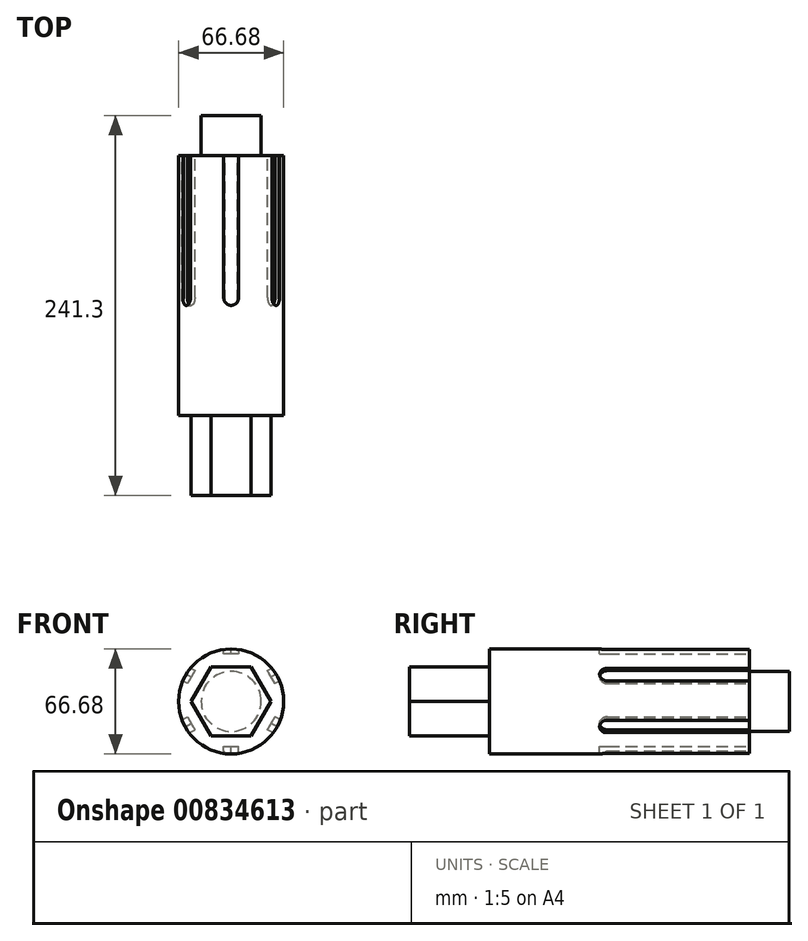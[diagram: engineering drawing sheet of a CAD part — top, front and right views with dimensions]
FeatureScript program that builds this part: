
annotation { "Feature Type Name" : "Feature", "Feature Type Description" : "" }
export const myFeature = defineFeature(function(context is Context, id is Id, definition is map)
    precondition{}
    {
        {
            var Q0;
            Q0=qCreatedBy(makeId("Front.planeOp"),FACE);
            var sketch = newSketch(context, id + "F0", { "sketchPlane" : qUnion([Q0])});
            skCircle(sketch, "E0.cCircle", {"center": v(0, 0) * mm, "radius": 25.4 * mm, "construction": true});
            skLineSegment(sketch, "E0.0", {"start": v(12.7, -22) * mm, "end": v(-12.7, -22) * mm});
            skLineSegment(sketch, "E0.1", {"start": v(-12.7, -22) * mm, "end": v(-25.4, 0) * mm});
            skLineSegment(sketch, "E0.2", {"start": v(-25.4, 0) * mm, "end": v(-12.7, 22) * mm});
            skLineSegment(sketch, "E0.3", {"start": v(-12.7, 22) * mm, "end": v(12.7, 22) * mm});
            skLineSegment(sketch, "E0.4", {"start": v(12.7, 22) * mm, "end": v(25.4, 0) * mm});
            skLineSegment(sketch, "E0.5", {"start": v(25.4, 0) * mm, "end": v(12.7, -22) * mm});
            skSolve(sketch);
        }
        {
            var Q0;
            Q0=makeQuery(id+"F0.imprint","IMPRINT",FACE,{"disambiguationData":[TD([[makeQuery(id+"F0.imprint","IMPRINT",EDGE,{"derivedFrom":sQuery(id+"F0.wireOp",EDGE,"E0.0")}),-1.0]])]});
            extrude(context, id + "F1", {"entities" : qUnion([Q0]), "depth" : 50.8 * mm, "offsetDistance" : 25.4 * mm});
        }
        {
            var Q0;
            Q0=makeQuery(id+"F1.opExtrude","CAP_FACE",FACE,{"disambiguationData":[OSD([sQuery(id+"F0.wireOp",EDGE,"E0.0"),sQuery(id+"F0.wireOp",EDGE,"E0.1"),sQuery(id+"F0.wireOp",EDGE,"E0.2"),sQuery(id+"F0.wireOp",EDGE,"E0.3"),sQuery(id+"F0.wireOp",EDGE,"E0.4"),sQuery(id+"F0.wireOp",EDGE,"E0.5")])],"isStart":true});
            var sketch = newSketch(context, id + "F2", { "sketchPlane" : qUnion([Q0])});
            skCircle(sketch, "E1", {"center": v(0, 0) * mm, "radius": 33.34 * mm});
            skSolve(sketch);
        }
        {
            var Q0;
            Q0 = qSketchRegion(id + "F2", true);
            extrude(context, id + "F3", {"entities" : qUnion([Q0]), "operationType" : NewBodyOperationType.ADD, "depth" : 165.1 * mm, "offsetDistance" : 25.4 * mm});
        }
        {
            var Q0;
            Q0=makeQuery(id+"F3.opExtrude","CAP_FACE",FACE,{"disambiguationData":[OSD([sQuery(id+"F2.wireOp",EDGE,"E1")])],"isStart":false});
            var sketch = newSketch(context, id + "F4", { "sketchPlane" : qUnion([Q0])});
            skCircle(sketch, "E2", {"center": v(0, 0) * mm, "radius": 19.05 * mm});
            skSolve(sketch);
        }
        {
            var Q0;
            Q0 = qSketchRegion(id + "F4", true);
            extrude(context, id + "F5", {"entities" : qUnion([Q0]), "operationType" : NewBodyOperationType.ADD, "depth" : 25.4 * mm, "offsetDistance" : 25.4 * mm});
        }
        {
            var Q0;
            Q0=makeQuery(id+"F3.opExtrude","CAP_FACE",FACE,{"disambiguationData":[OSD([sQuery(id+"F2.wireOp",EDGE,"E1")])],"isStart":false});
            var sketch = newSketch(context, id + "F6", { "sketchPlane" : qUnion([Q0])});
            skLineSegment(sketch, "E3", {"start": v(0, 0) * mm, "end": v(0, 60.33) * mm, "construction": true});
            skLineSegment(sketch, "E4", {"start": v(-4.76, 33) * mm, "end": v(-4.76, 30.16) * mm});
            skLineSegment(sketch, "E5", {"start": v(-4.76, 30.16) * mm, "end": v(4.76, 30.16) * mm});
            skLineSegment(sketch, "E6", {"start": v(4.76, 30.16) * mm, "end": v(4.76, 33) * mm});
            skPoint(sketch, "E7", {"position": v(0, 30.16) * mm});
            skArc(sketch, "E8", {"start": v(4.76, 33) * mm, "mid": v(0, 36.72) * mm, "end": v(-4.76, 33) * mm});
            skPoint(sketch, "E9", {"position": v(0, 33.34) * mm});
            skLineSegment(sketch, "E10.1.0", {"start": v(25.51, 21.02) * mm, "end": v(23.06, 19.6) * mm});
            skLineSegment(sketch, "E10.1.1", {"start": v(23.06, 19.6) * mm, "end": v(27.82, 11.35) * mm});
            skArc(sketch, "E10.1.2", {"start": v(30.27, 12.77) * mm, "mid": v(31.12, 18.75) * mm, "end": v(25.51, 21.02) * mm});
            skLineSegment(sketch, "E10.1.3", {"start": v(-0.68, 0.4) * mm, "end": v(51.56, 30.56) * mm, "construction": true});
            skLineSegment(sketch, "E10.2.0", {"start": v(30.27, -11.2) * mm, "end": v(27.82, -9.78) * mm});
            skLineSegment(sketch, "E10.2.1", {"start": v(27.82, -9.78) * mm, "end": v(23.06, -18.02) * mm});
            skArc(sketch, "E10.2.2", {"start": v(25.51, -19.44) * mm, "mid": v(31.12, -17.18) * mm, "end": v(30.27, -11.2) * mm});
            skLineSegment(sketch, "E10.2.3", {"start": v(-0.68, 1.18) * mm, "end": v(51.56, -28.98) * mm, "construction": true});
            skLineSegment(sketch, "E10.3.0", {"start": v(4.76, -31.42) * mm, "end": v(4.76, -28.59) * mm});
            skLineSegment(sketch, "E10.3.1", {"start": v(4.76, -28.59) * mm, "end": v(-4.76, -28.59) * mm});
            skArc(sketch, "E10.3.2", {"start": v(-4.76, -31.42) * mm, "mid": v(0, -35.14) * mm, "end": v(4.76, -31.42) * mm});
            skLineSegment(sketch, "E10.3.3", {"start": v(0, 1.57) * mm, "end": v(0, -58.75) * mm, "construction": true});
            skLineSegment(sketch, "E10.4.0", {"start": v(-25.51, -19.44) * mm, "end": v(-23.06, -18.02) * mm});
            skLineSegment(sketch, "E10.4.1", {"start": v(-23.06, -18.02) * mm, "end": v(-27.82, -9.78) * mm});
            skArc(sketch, "E10.4.2", {"start": v(-30.27, -11.2) * mm, "mid": v(-31.12, -17.18) * mm, "end": v(-25.51, -19.44) * mm});
            skLineSegment(sketch, "E10.4.3", {"start": v(0.68, 1.18) * mm, "end": v(-51.56, -28.98) * mm, "construction": true});
            skLineSegment(sketch, "E10.5.0", {"start": v(-30.27, 12.77) * mm, "end": v(-27.82, 11.35) * mm});
            skLineSegment(sketch, "E10.5.1", {"start": v(-27.82, 11.35) * mm, "end": v(-23.06, 19.6) * mm});
            skArc(sketch, "E10.5.2", {"start": v(-25.51, 21.02) * mm, "mid": v(-31.12, 18.75) * mm, "end": v(-30.27, 12.77) * mm});
            skLineSegment(sketch, "E10.5.3", {"start": v(0.68, 0.4) * mm, "end": v(-51.56, 30.56) * mm, "construction": true});
            skPoint(sketch, "E10.center", {"position": v(0, 0.79) * mm});
            skLineSegment(sketch, "E10.anchor1", {"start": v(0, 0.79) * mm, "end": v(-4.76, 30.16) * mm, "construction": true});
            skLineSegment(sketch, "E10.anchor2", {"start": v(0, 0.79) * mm, "end": v(-27.82, 11.35) * mm, "construction": true});
            skLineSegment(sketch, "E11", {"start": v(-23.06, 19.6) * mm, "end": v(-25.51, 21.02) * mm});
            skLineSegment(sketch, "E12", {"start": v(27.82, 11.35) * mm, "end": v(30.27, 12.77) * mm});
            skLineSegment(sketch, "E13", {"start": v(-4.76, -31.42) * mm, "end": v(-4.76, -28.59) * mm});
            skLineSegment(sketch, "E14", {"start": v(-30.27, -11.2) * mm, "end": v(-27.82, -9.78) * mm});
            skLineSegment(sketch, "E15", {"start": v(25.51, -19.44) * mm, "end": v(23.06, -18.02) * mm});
            skSolve(sketch);
        }
        {
            var Q0;
            Q0 = qSketchRegion(id + "F6", true);
            extrude(context, id + "F7", {"entities" : qUnion([Q0]), "operationType" : NewBodyOperationType.REMOVE, "oppositeDirection" : true, "depth" : 95.25 * mm, "offsetDistance" : 25.4 * mm});
        }
        {
            var Q0;
            Q0=makeQuery(id+"F7.boolean.opBoolean","COPY",EDGE,{"derivedFrom":makeQuery(id+"F7.opExtrude","CAP_EDGE",EDGE,{"disambiguationData":[OSD([sQuery(id+"F6.wireOp",EDGE,"E10.1.0")])],"isStart":false})});
            var Q1;
            Q1=makeQuery(id+"F7.boolean.opBoolean","COPY",EDGE,{"derivedFrom":makeQuery(id+"F7.opExtrude","CAP_EDGE",EDGE,{"disambiguationData":[OSD([sQuery(id+"F6.wireOp",EDGE,"E12")])],"isStart":false})});
            var Q2;
            Q2=makeQuery(id+"F7.boolean.opBoolean","COPY",EDGE,{"derivedFrom":makeQuery(id+"F7.opExtrude","CAP_EDGE",EDGE,{"disambiguationData":[OSD([sQuery(id+"F6.wireOp",EDGE,"E4")])],"isStart":false})});
            var Q3;
            Q3=makeQuery(id+"F7.boolean.opBoolean","COPY",EDGE,{"derivedFrom":makeQuery(id+"F7.opExtrude","CAP_EDGE",EDGE,{"disambiguationData":[OSD([sQuery(id+"F6.wireOp",EDGE,"E6")])],"isStart":false})});
            var Q4;
            Q4=makeQuery(id+"F7.boolean.opBoolean","COPY",EDGE,{"derivedFrom":makeQuery(id+"F7.opExtrude","CAP_EDGE",EDGE,{"disambiguationData":[OSD([sQuery(id+"F6.wireOp",EDGE,"E11")])],"isStart":false})});
            var Q5;
            Q5=makeQuery(id+"F7.boolean.opBoolean","COPY",EDGE,{"derivedFrom":makeQuery(id+"F7.opExtrude","CAP_EDGE",EDGE,{"disambiguationData":[OSD([sQuery(id+"F6.wireOp",EDGE,"E10.5.0")])],"isStart":false})});
            var Q6;
            Q6=makeQuery(id+"F7.boolean.opBoolean","COPY",EDGE,{"derivedFrom":makeQuery(id+"F7.opExtrude","CAP_EDGE",EDGE,{"disambiguationData":[OSD([sQuery(id+"F6.wireOp",EDGE,"E14")])],"isStart":false})});
            var Q7;
            Q7=makeQuery(id+"F7.boolean.opBoolean","COPY",EDGE,{"derivedFrom":makeQuery(id+"F7.opExtrude","CAP_EDGE",EDGE,{"disambiguationData":[OSD([sQuery(id+"F6.wireOp",EDGE,"E10.4.0")])],"isStart":false})});
            var Q8;
            Q8=makeQuery(id+"F7.boolean.opBoolean","COPY",EDGE,{"derivedFrom":makeQuery(id+"F7.opExtrude","CAP_EDGE",EDGE,{"disambiguationData":[OSD([sQuery(id+"F6.wireOp",EDGE,"E13")])],"isStart":false})});
            var Q9;
            Q9=makeQuery(id+"F7.boolean.opBoolean","COPY",EDGE,{"derivedFrom":makeQuery(id+"F7.opExtrude","CAP_EDGE",EDGE,{"disambiguationData":[OSD([sQuery(id+"F6.wireOp",EDGE,"E10.3.0")])],"isStart":false})});
            var Q10;
            Q10=makeQuery(id+"F7.boolean.opBoolean","COPY",EDGE,{"derivedFrom":makeQuery(id+"F7.opExtrude","CAP_EDGE",EDGE,{"disambiguationData":[OSD([sQuery(id+"F6.wireOp",EDGE,"E15")])],"isStart":false})});
            var Q11;
            Q11=makeQuery(id+"F7.boolean.opBoolean","COPY",EDGE,{"derivedFrom":makeQuery(id+"F7.opExtrude","CAP_EDGE",EDGE,{"disambiguationData":[OSD([sQuery(id+"F6.wireOp",EDGE,"E10.2.0")])],"isStart":false})});
            fillet(context, id + "F8", {"entities" : qUnion([Q0, Q1, Q2, Q3, Q4, Q5, Q6, Q7, Q8, Q9, Q10, Q11]), "radius" : 5.08 * mm, "tangentPropagation" : true, "allowEdgeOverflow" : false});
        }
    });
